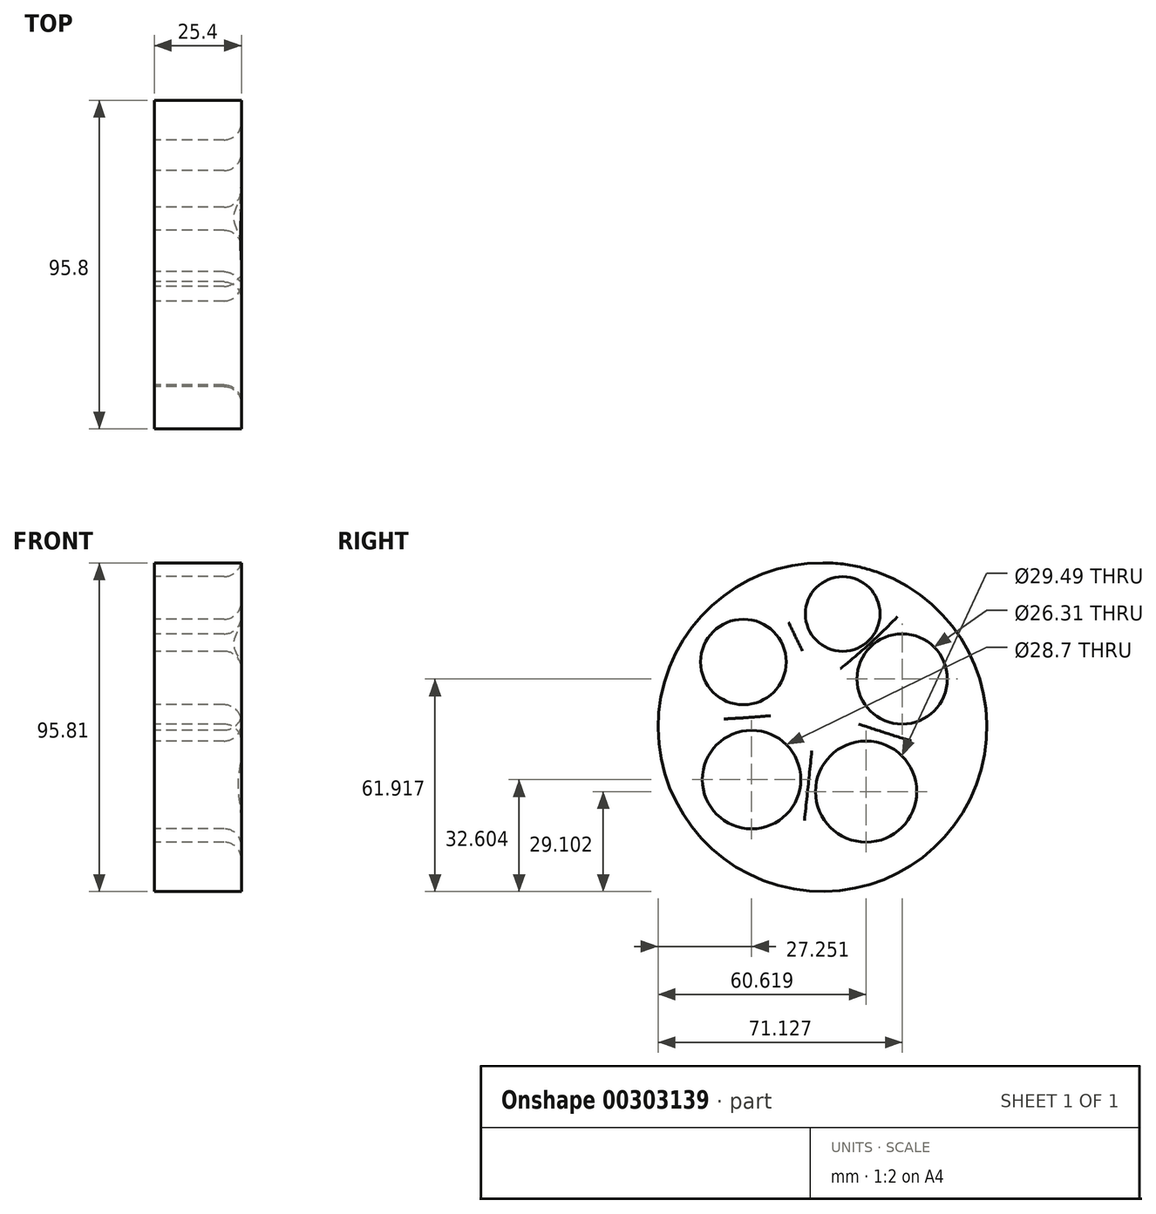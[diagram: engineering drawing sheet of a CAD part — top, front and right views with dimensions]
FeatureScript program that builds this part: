
annotation { "Feature Type Name" : "Feature", "Feature Type Description" : "" }
export const myFeature = defineFeature(function(context is Context, id is Id, definition is map)
    precondition{}
    {
        {
            var Q0;
            Q0=qCreatedBy(makeId("Right.planeOp"),FACE);
            var sketch = newSketch(context, id + "F0", { "sketchPlane" : qUnion([Q0])});
            skCircle(sketch, "E0", {"center": v(0.37, -0.18) * mm, "radius": 47.9 * mm});
            skCircle(sketch, "E1", {"center": v(0.18, 0.18) * mm, "radius": 44.04 * mm});
            skCircle(sketch, "E2", {"center": v(-20.28, -15.49) * mm, "radius": 14.35 * mm});
            skCircle(sketch, "E3", {"center": v(-22.68, 18.8) * mm, "radius": 12.47 * mm});
            skCircle(sketch, "E4", {"center": v(6.27, 32.82) * mm, "radius": 10.88 * mm});
            skCircle(sketch, "E5", {"center": v(13.09, -18.99) * mm, "radius": 14.74 * mm});
            skCircle(sketch, "E6", {"center": v(23.6, 13.83) * mm, "radius": 13.15 * mm});
            skSolve(sketch);
        }
        {
            var Q0;
            Q0=makeQuery(id+"F0.imprint","IMPRINT",FACE,{"disambiguationData":[TD([[makeQuery(id+"F0.imprint","IMPRINT",EDGE,{"derivedFrom":sQuery(id+"F0.wireOp",EDGE,"E2")}),-1.0]])]});
            var Q1;
            Q1=makeQuery(id+"F0.imprint","IMPRINT",FACE,{"disambiguationData":[TD([[makeQuery(id+"F0.imprint","IMPRINT",EDGE,{"derivedFrom":sQuery(id+"F0.wireOp",EDGE,"E0")}),1.0]])]});
            extrude(context, id + "F1", {"entities" : qUnion([Q0, Q1]), "depth" : 25.4 * mm});
        }
        {
            var Q0;
            Q0=makeQuery(id+"F1.opExtrude","CAP_EDGE",EDGE,{"disambiguationData":[OSD([sQuery(id+"F0.wireOp",EDGE,"E3")])],"isStart":false});
            var Q1;
            Q1=makeQuery(id+"F1.opExtrude","CAP_EDGE",EDGE,{"disambiguationData":[OSD([sQuery(id+"F0.wireOp",EDGE,"E4")])],"isStart":false});
            var Q2;
            Q2=makeQuery(id+"F1.opExtrude","CAP_EDGE",EDGE,{"disambiguationData":[OSD([sQuery(id+"F0.wireOp",EDGE,"E6")])],"isStart":false});
            var Q3;
            Q3=makeQuery(id+"F1.opExtrude","CAP_EDGE",EDGE,{"disambiguationData":[OSD([sQuery(id+"F0.wireOp",EDGE,"E5")])],"isStart":false});
            var Q4;
            Q4=makeQuery(id+"F1.opExtrude","CAP_EDGE",EDGE,{"disambiguationData":[OSD([sQuery(id+"F0.wireOp",EDGE,"E2")])],"isStart":false});
            fillet(context, id + "F2", {"entities" : qUnion([Q0, Q1, Q2, Q3, Q4]), "radius" : 5.08 * mm, "tangentPropagation" : true, "allowEdgeOverflow" : false});
        }
    });
